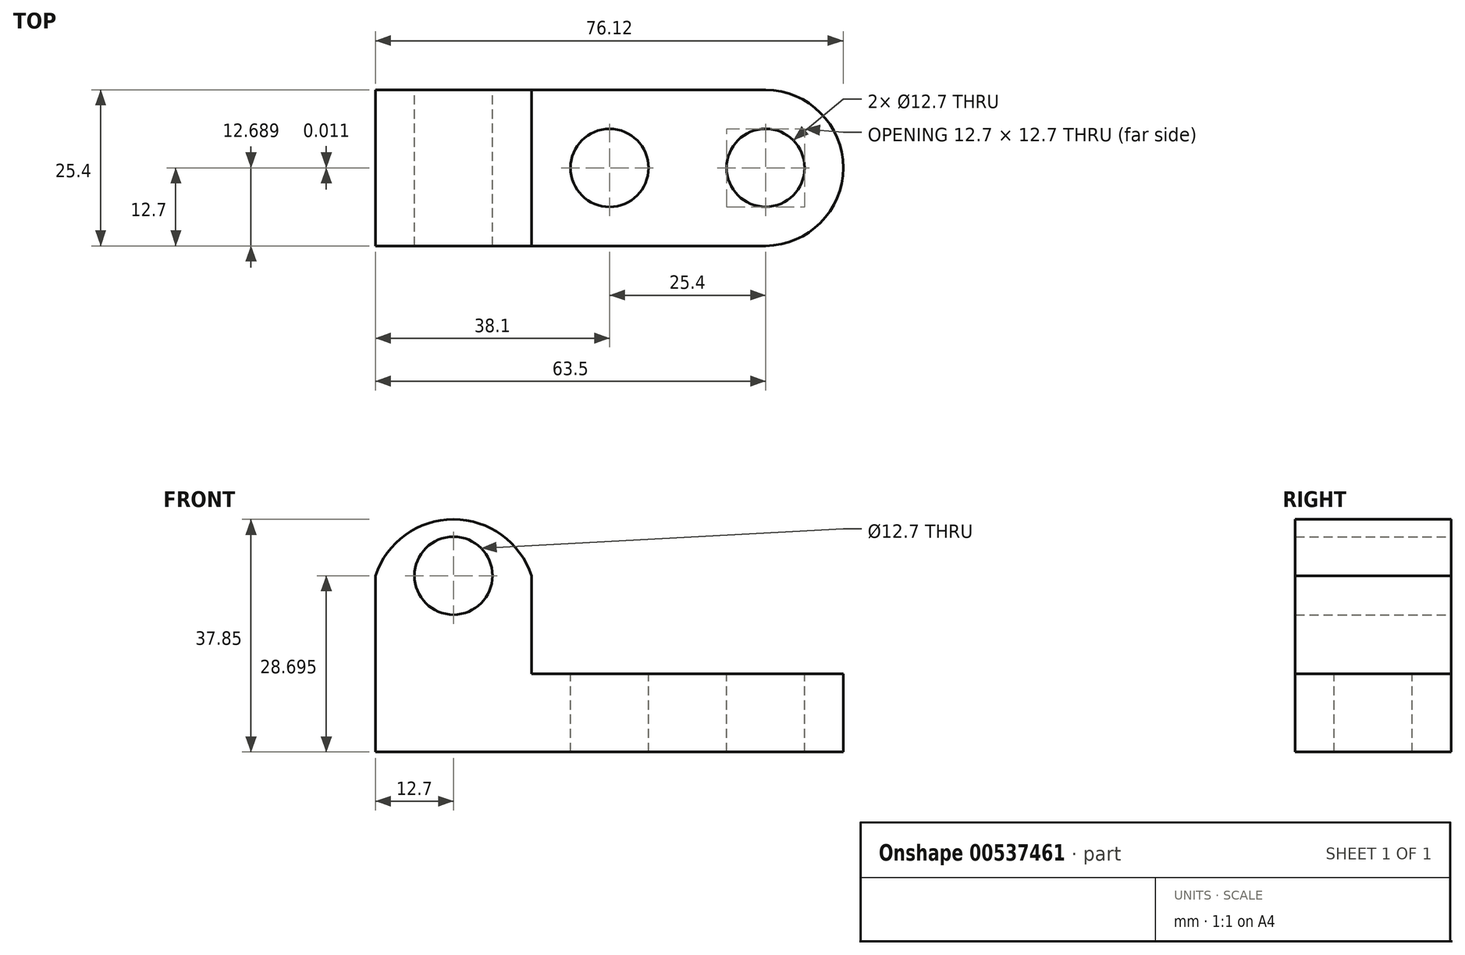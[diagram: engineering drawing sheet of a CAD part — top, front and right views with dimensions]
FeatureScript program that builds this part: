
annotation { "Feature Type Name" : "Feature", "Feature Type Description" : "" }
export const myFeature = defineFeature(function(context is Context, id is Id, definition is map)
    precondition{}
    {
        {
            var Q0;
            Q0=qCreatedBy(makeId("Front.planeOp"),FACE);
            var sketch = newSketch(context, id + "F0", { "sketchPlane" : qUnion([Q0])});
            skLineSegment(sketch, "E0", {"start": v(0, 0) * mm, "end": v(0, 38.1) * mm});
            skLineSegment(sketch, "E1", {"start": v(0, 38.1) * mm, "end": v(25.4, 38.1) * mm});
            skLineSegment(sketch, "E2", {"start": v(25.4, 38.1) * mm, "end": v(25.4, 12.7) * mm});
            skLineSegment(sketch, "E3", {"start": v(25.4, 12.7) * mm, "end": v(76.2, 12.7) * mm});
            skLineSegment(sketch, "E4", {"start": v(76.2, 12.7) * mm, "end": v(76.2, 0) * mm});
            skLineSegment(sketch, "E5", {"start": v(76.2, 0) * mm, "end": v(0, 0) * mm});
            skCircle(sketch, "E6", {"center": v(12.7, 28.7) * mm, "radius": 6.35 * mm});
            skArc(sketch, "E7", {"start": v(25.4, 28.7) * mm, "mid": v(12.7, 37.85) * mm, "end": v(0, 28.7) * mm});
            skSolve(sketch);
        }
        {
            var Q0;
            {var subQ0=sQuery(id+"F0.wireOp",EDGE,"E3");Q0=makeQuery(id+"F0.imprint","IMPRINT",FACE,{"disambiguationData":[TD([[makeQuery(id+"F0.imprint","IMPRINT",EDGE,{"derivedFrom":subQ0}),-1.0]])]});}
            extrude(context, id + "F1", {"entities" : qUnion([Q0]), "depth" : 25.4 * mm, "offsetDistance" : 25.4 * mm});
        }
        {
            var Q0;
            Q0=makeQuery(id+"F1.opExtrude","SWEPT_FACE",FACE,{"disambiguationData":[OSD([sQuery(id+"F0.wireOp",EDGE,"E3")])]});
            var sketch = newSketch(context, id + "F2", { "sketchPlane" : qUnion([Q0])});
            skCircle(sketch, "E8", {"center": v(38.1, -12.71) * mm, "radius": 6.35 * mm});
            skCircle(sketch, "E9", {"center": v(63.5, -12.7) * mm, "radius": 6.35 * mm});
            skLineSegment(sketch, "E10", {"start": v(38.1, -6.36) * mm, "end": v(63.5, -6.35) * mm});
            skLineSegment(sketch, "E11", {"start": v(63.5, -6.35) * mm, "end": v(63.5, -19.05) * mm});
            skLineSegment(sketch, "E12", {"start": v(63.5, -19.05) * mm, "end": v(38.1, -19.07) * mm});
            skLineSegment(sketch, "E13", {"start": v(38.1, -19.07) * mm, "end": v(38.1, -6.36) * mm});
            skSolve(sketch);
        }
        {
            var Q0;
            {var subQ1=sQuery(id+"F2.wireOp",EDGE,"E10");Q0=makeQuery(id+"F2.imprint","IMPRINT",FACE,{"disambiguationData":[TD([[makeQuery(id+"F2.imprint","IMPRINT",EDGE,{"derivedFrom":subQ1}),-1.0]])]});}
            var Q1;
            {var subQ0=sQuery(id+"F2.wireOp",EDGE,"E13");var subQ1=sQuery(id+"F2.wireOp",EDGE,"E8");var subQ3=makeQuery(id+"F2.imprint","INTERSECT",VERTEX,{"derivedFrom":[subQ1,subQ0]});Q1=makeQuery(id+"F2.imprint","IMPRINT",FACE,{"disambiguationData":[TD([[makeQuery(id+"F2.imprint","IMPRINT",EDGE,{"disambiguationData":[TD([[subQ3,-1.0]])],"derivedFrom":subQ1}),1.0]])]});}
            var Q2;
            {var subQ0=sQuery(id+"F2.wireOp",EDGE,"E13");var subQ1=sQuery(id+"F2.wireOp",EDGE,"E8");var subQ3=makeQuery(id+"F2.imprint","INTERSECT",VERTEX,{"derivedFrom":[subQ1,subQ0]});Q2=makeQuery(id+"F2.imprint","IMPRINT",FACE,{"disambiguationData":[TD([[makeQuery(id+"F2.imprint","IMPRINT",EDGE,{"disambiguationData":[TD([[subQ3,1.0]])],"derivedFrom":subQ1}),1.0]])]});}
            var Q3;
            {var subQ0=sQuery(id+"F2.wireOp",EDGE,"E11");Q3=makeQuery(id+"F2.imprint","IMPRINT",FACE,{"disambiguationData":[TD([[makeQuery(id+"F2.imprint","IMPRINT",EDGE,{"derivedFrom":subQ0}),1.0]])]});}
            var Q4;
            {var subQ2=sQuery(id+"F2.wireOp",EDGE,"E11");Q4=makeQuery(id+"F2.imprint","IMPRINT",FACE,{"disambiguationData":[TD([[makeQuery(id+"F2.imprint","IMPRINT",EDGE,{"derivedFrom":subQ2}),-1.0]])]});}
            extrude(context, id + "F3", {"entities" : qUnion([Q0, Q1, Q2, Q3, Q4]), "operationType" : NewBodyOperationType.REMOVE, "oppositeDirection" : true, "depth" : 25.4 * mm, "offsetDistance" : 25.4 * mm});
        }
        {
            var Q0;
            Q0=makeQuery(id+"F1.opExtrude","SWEPT_FACE",FACE,{"disambiguationData":[OSD([sQuery(id+"F0.wireOp",EDGE,"E3")])]});
            var sketch = newSketch(context, id + "F4", { "sketchPlane" : qUnion([Q0])});
            skArc(sketch, "E14", {"start": v(63.5, -25.4) * mm, "mid": v(76.12, -12.7) * mm, "end": v(63.5, 0) * mm});
            skSolve(sketch);
        }
        {
            var Q0;
            Q0 = qSketchRegion(id + "F4", true);
            var Q1;
            {var subQ0=sQuery(id+"F4.wireOp",EDGE,"E14");Q1=makeQuery(id+"F4.imprint","IMPRINT",FACE,{"disambiguationData":[TD([[makeQuery(id+"F4.imprint","IMPRINT",EDGE,{"derivedFrom":subQ0}),-1.0]])]});}
            extrude(context, id + "F5", {"entities" : qUnion([Q0, Q1]), "operationType" : NewBodyOperationType.REMOVE, "oppositeDirection" : true, "depth" : 25.4 * mm, "offsetDistance" : 25.4 * mm});
        }
    });
